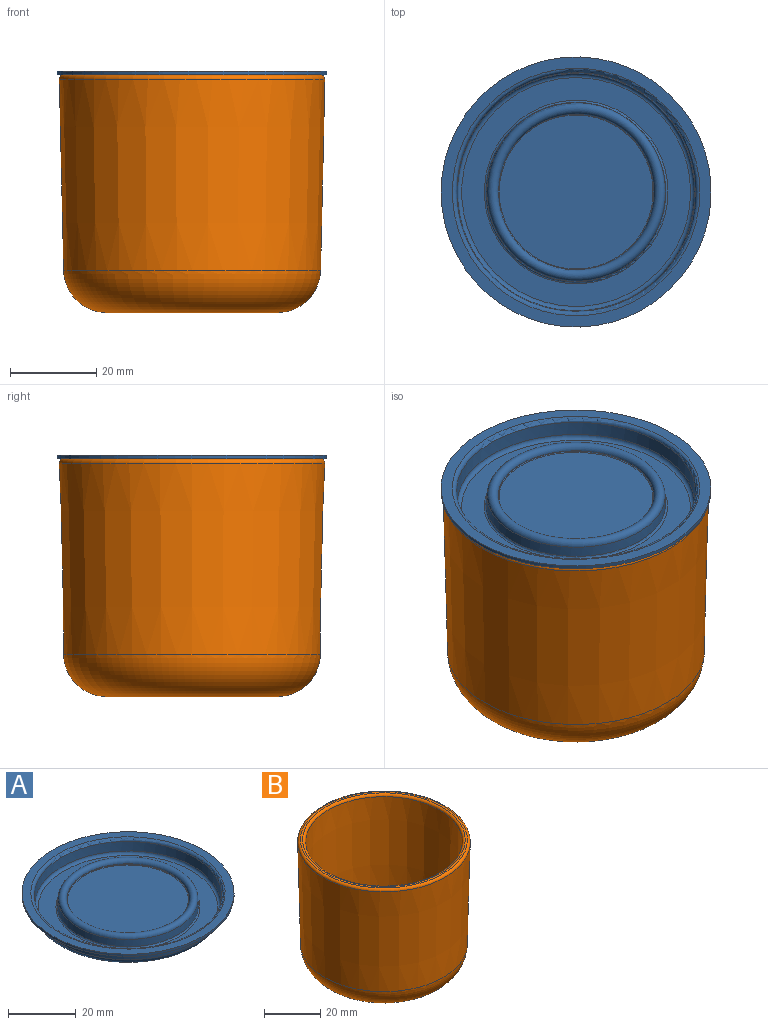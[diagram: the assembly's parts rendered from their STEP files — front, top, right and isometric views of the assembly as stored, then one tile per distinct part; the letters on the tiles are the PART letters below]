
ASSEMBLY  parts=2 mates=1
PART A: 22 faces, bbox 62.5x62.5x6 mm
  f0: plane 35.62x35.62mm, normal (0,0,-1), area 996.5mm2, adj f18
  f1: cone r=18.76mm half-angle=3deg, axis (0,0,1), area 9.3mm2, adj f2,f18
  f2: torus R=19.31mm, axis (0,0,-1), area 184.3mm2, adj f1,f3
  f3: cone r=19.81mm half-angle=3deg, axis (0,0,-1), area 347.6mm2, adj f2,f17
  f4: plane 52.56x52.56mm, normal (0,0,-1), area 790mm2, adj f15,f17
  f5: cone r=28.18mm half-angle=3deg, axis (0,0,1), area 589.7mm2, adj f6,f15
  f6: plane 62.5x62.5mm, normal (0,0,-1), area 525.1mm2, adj f5,f7
  f7: cylinder r=31.25mm len=62.5mm, axis (0,0,-1), area 157.1mm2, adj f6,f8
  f8: plane 62.5x62.5mm, normal (0,0,1), area 491.1mm2, adj f7,f21
  f9: cone r=27.69mm half-angle=3deg, axis (0,0,1), area 572.9mm2, adj f16,f21
  f10: plane 52.94x52.94mm, normal (0,0,1), area 783.7mm2, adj f16,f20
  f11: cone r=20.77mm half-angle=3deg, axis (0,0,-1), area 324.5mm2, adj f12,f20
  f12: torus R=19.31mm, axis (0,0,-1), area 479.1mm2, adj f11,f13
  f13: cone r=18mm half-angle=3deg, axis (0,0,1), area 8.9mm2, adj f12,f19
  f14: plane 35.62x35.62mm, normal (0,0,1), area 996.5mm2, adj f19
  f15: torus R=26.28mm, axis (0,0,-1), area 525.3mm2, adj f4,f5
  f16: torus R=26.47mm, axis (0,0,1), area 258.5mm2, adj f9,f10
  f17: torus R=20.96mm, axis (0,0,-1), area 194mm2, adj f3,f4
  f18: torus R=17.81mm, axis (0,0,-1), area 175.9mm2, adj f0,f1
  f19: torus R=17.81mm, axis (0,0,-1), area 34.2mm2, adj f13,f14
  f20: torus R=21.24mm, axis (0,0,1), area 99.8mm2, adj f10,f11
  f21: torus R=28.64mm, axis (0,0,1), area 267.3mm2, adj f8,f9
PART B: 13 faces, bbox 66.5x66.5x55 mm
  f0: plane 59.45x59.45mm, normal (0,0,1), area 147.3mm2, adj f2,f3
  f1: torus R=17.04mm, axis (0,0,-1), area 2271.4mm2, adj f7,f8
  f2: torus R=29.73mm, axis (0,0,-1), area 304.1mm2, adj f0,f4
  f3: torus R=28.93mm, axis (0,0,-1), area 275.2mm2, adj f0,f7
  f4: cone r=29.49mm half-angle=1.3deg, axis (0,0,1), area 8396mm2, adj f2,f5
  f5: torus R=19.72mm, axis (0,0,1), area 2531.5mm2, adj f4,f6
  f6: plane 39.43x39.43mm, normal (0,0,-1), area 30.8mm2, adj f5,f12
  f7: cone r=27.95mm half-angle=1.3deg, axis (0,0,1), area 6693.6mm2, adj f1,f3
  f8: plane 34.09x34.09mm, normal (0,0,1), area 912.5mm2, adj f1
  f9: plane 34.55x34.55mm, normal (0,0,-1), area 937.5mm2, adj f11
  f10: cone r=17.74mm half-angle=40deg, axis (0,0,-1), area 118.4mm2, adj f11,f12
  f11: torus R=17.28mm, axis (0,0,1), area 97mm2, adj f9,f10
  f12: torus R=19.47mm, axis (0,0,1), area 104.5mm2, adj f6,f10
PLACE A t=(-16.16,17.61,43.51)mm
PLACE B t=(-16.16,17.61,-6.29)mm
MATE parallel B.f1 <-> A.f1  axis (0,0,1) through (-16.16,17.61,48.71)mm
